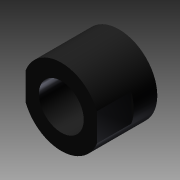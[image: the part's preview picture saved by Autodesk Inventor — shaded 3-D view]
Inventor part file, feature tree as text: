
AUTODESK INVENTOR PART (.ipt)
format: ipt  version: 2011 (Build 150239000, 239)  size: 87,552 bytes
history: native  units: in
note: dims shown in document units (in); Inventor stores cm internally (conversion verified against a paired STEP export)
features: extrude x2, sketch x2
ambient origin geometry x8: Origin, YZ Plane, XZ Plane, XY Plane, X Axis, Y Axis, Z Axis, Center Point
bodies: Solid1 (feature_tree)
feature tree (4):
  extrude  "Extrusion1"  Depth=0.425in
  extrude  "Extrusion2"  Depth=0.675in
  sketch  "Sketch1"  dims[d0=0.725in d1=0.425in]
  sketch  "Sketch2"  dims[d2=0.222in d3=0.0in d4=0.675in d5=0.325in d6=0.0in]
